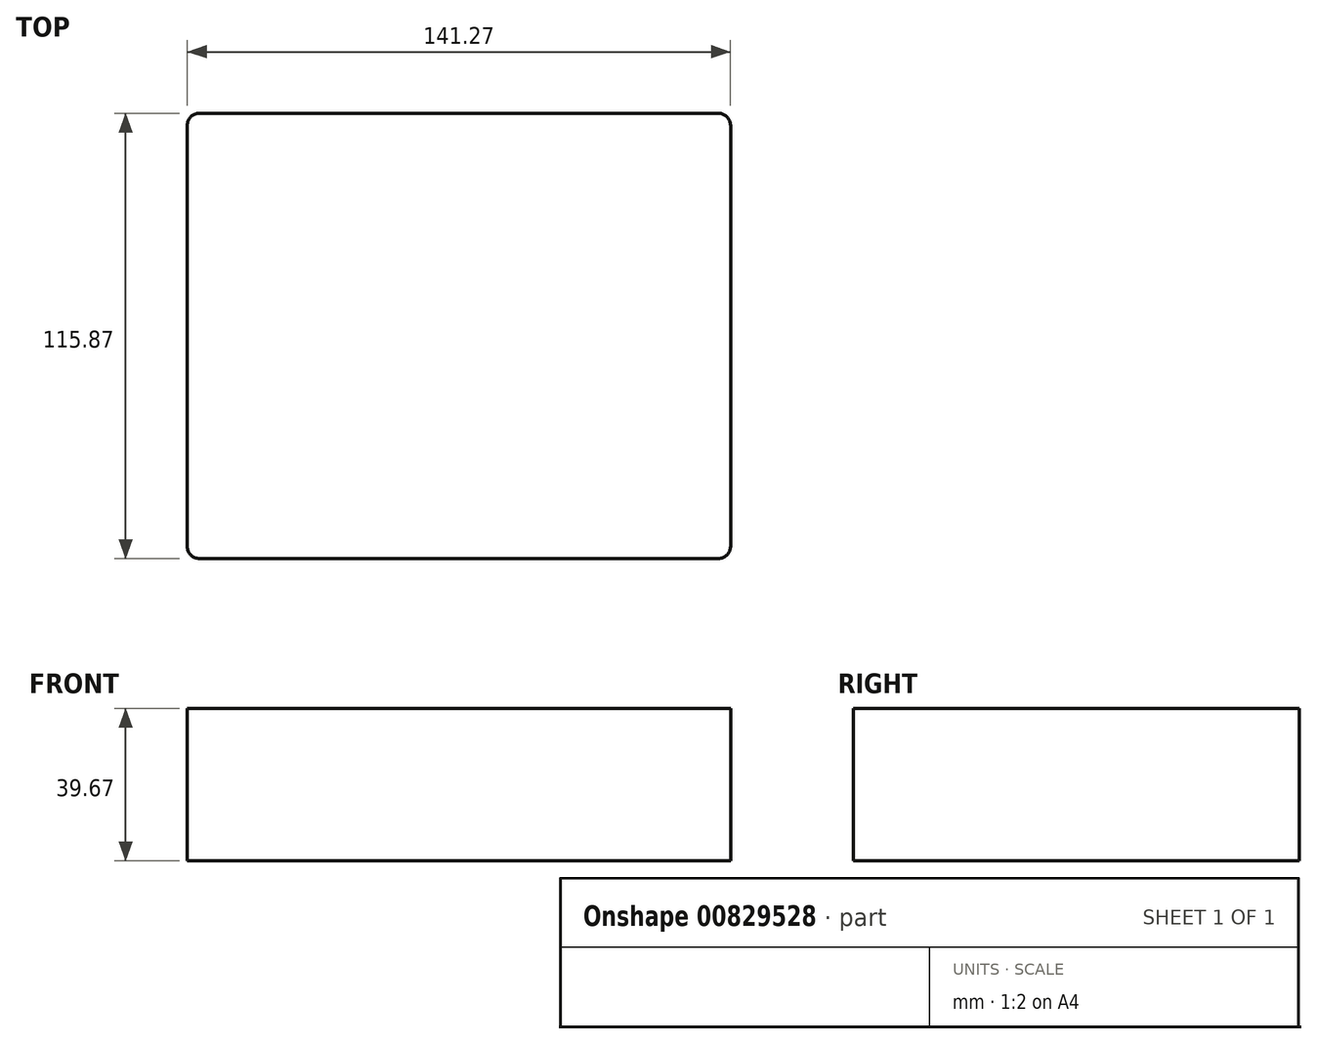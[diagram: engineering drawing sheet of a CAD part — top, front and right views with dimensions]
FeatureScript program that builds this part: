
annotation { "Feature Type Name" : "Feature", "Feature Type Description" : "" }
export const myFeature = defineFeature(function(context is Context, id is Id, definition is map)
    precondition{}
    {
        {
            var Q0;
            Q0=qCreatedBy(makeId("Top.planeOp"),FACE);
            var sketch = newSketch(context, id + "F0", { "sketchPlane" : qUnion([Q0])});
            skLineSegment(sketch, "E0.bottom", {"start": v(3.17, 0) * mm, "end": v(138.1, 0) * mm});
            skLineSegment(sketch, "E0.top", {"start": v(3.17, 115.87) * mm, "end": v(138.1, 115.87) * mm});
            skLineSegment(sketch, "E0.left", {"start": v(0, 3.17) * mm, "end": v(0, 112.7) * mm});
            skLineSegment(sketch, "E0.right", {"start": v(141.27, 3.17) * mm, "end": v(141.27, 112.7) * mm});
            skPoint(sketch, "E1.visualSharp", {"position": v(0, 115.87) * mm});
            skArc(sketch, "E1.filletArc", {"start": v(3.17, 115.87) * mm, "mid": v(0.93, 114.94) * mm, "end": v(0, 112.7) * mm});
            skPoint(sketch, "E2.visualSharp", {"position": v(141.27, 115.87) * mm});
            skArc(sketch, "E2.filletArc", {"start": v(141.27, 112.7) * mm, "mid": v(140.34, 114.94) * mm, "end": v(138.1, 115.87) * mm});
            skPoint(sketch, "E3.visualSharp", {"position": v(141.27, 0) * mm});
            skArc(sketch, "E3.filletArc", {"start": v(138.1, 0) * mm, "mid": v(140.34, 0.93) * mm, "end": v(141.27, 3.17) * mm});
            skPoint(sketch, "E4.visualSharp", {"position": v(0, 0) * mm});
            skArc(sketch, "E4.filletArc", {"start": v(0, 3.17) * mm, "mid": v(0.93, 0.93) * mm, "end": v(3.17, 0) * mm});
            skSolve(sketch);
        }
        {
            var Q0;
            Q0=makeQuery(id+"F0.imprint","IMPRINT",FACE,{"disambiguationData":[TD([[makeQuery(id+"F0.imprint","IMPRINT",EDGE,{"derivedFrom":sQuery(id+"F0.wireOp",EDGE,"E0.bottom")}),1.0]])]});
            extrude(context, id + "F1", {"entities" : qUnion([Q0]), "depth" : 39.67 * mm, "offsetDistance" : 25.4 * mm});
        }
    });
